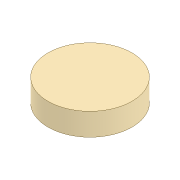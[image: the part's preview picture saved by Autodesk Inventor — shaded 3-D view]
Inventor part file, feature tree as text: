
AUTODESK INVENTOR PART (.ipt)
format: ipt  version: 2020 (Build 240168000, 168)  size: 75,264 bytes
history: native  units: mm
features: other x1, extrude x1, sketch x1
ambient origin geometry x8: Origin, YZ Plane, XZ Plane, XY Plane, X Axis, Y Axis, Z Axis, Center Point
bodies: Body1 (feature_tree)
feature tree (3):
  other  "Sólido1"
  extrude  "Extrusão1"  Depth=12.0mm TaperAngle=0.0deg
  sketch  "Esboço1"  dims[d0=44.9mm d1=12.0mm d2=0.0mm]
